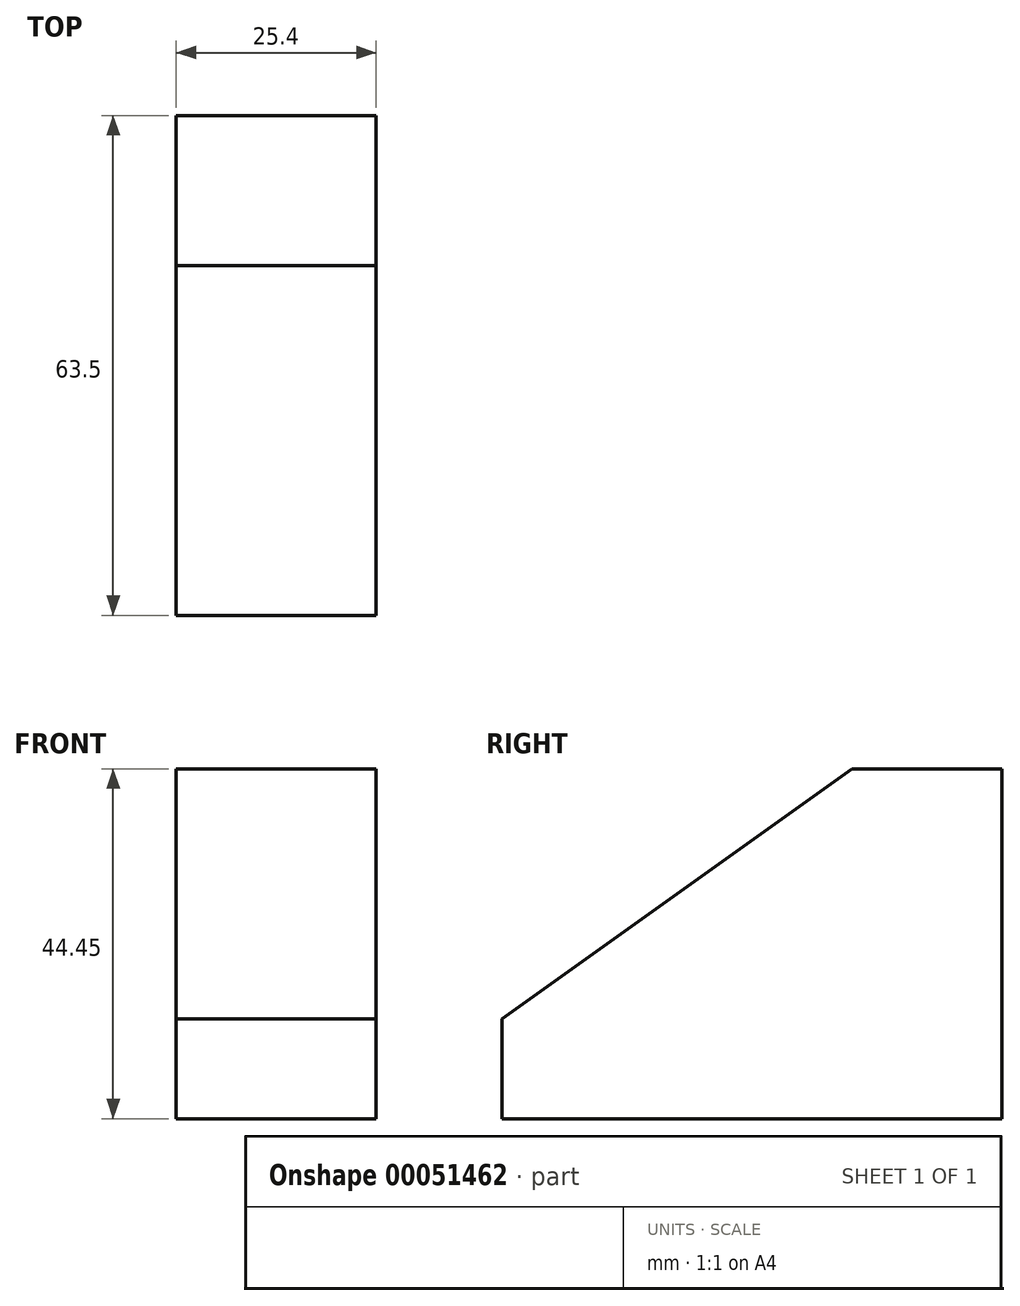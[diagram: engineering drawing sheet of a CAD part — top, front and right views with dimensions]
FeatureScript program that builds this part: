
annotation { "Feature Type Name" : "Feature", "Feature Type Description" : "" }
export const myFeature = defineFeature(function(context is Context, id is Id, definition is map)
    precondition{}
    {
        {
            var Q0;
            Q0=qCreatedBy(makeId("Right.planeOp"),FACE);
            var sketch = newSketch(context, id + "F0", { "sketchPlane" : qUnion([Q0])});
            skLineSegment(sketch, "E0", {"start": v(-51.48, -3.91) * mm, "end": v(-7.03, 27.84) * mm});
            skLineSegment(sketch, "E1", {"start": v(-7.03, 27.84) * mm, "end": v(12.02, 27.84) * mm});
            skLineSegment(sketch, "E2", {"start": v(12.02, 27.84) * mm, "end": v(12.02, -16.61) * mm});
            skLineSegment(sketch, "E3", {"start": v(-51.48, -3.91) * mm, "end": v(-51.48, -16.61) * mm});
            skLineSegment(sketch, "E4", {"start": v(-51.48, -16.61) * mm, "end": v(12.02, -16.61) * mm});
            skSolve(sketch);
        }
        {
            var Q0;
            Q0 = qSketchRegion(id + "F0", true);
            extrude(context, id + "F1", {"entities" : qUnion([Q0]), "depth" : 25.4 * mm});
        }
    });
